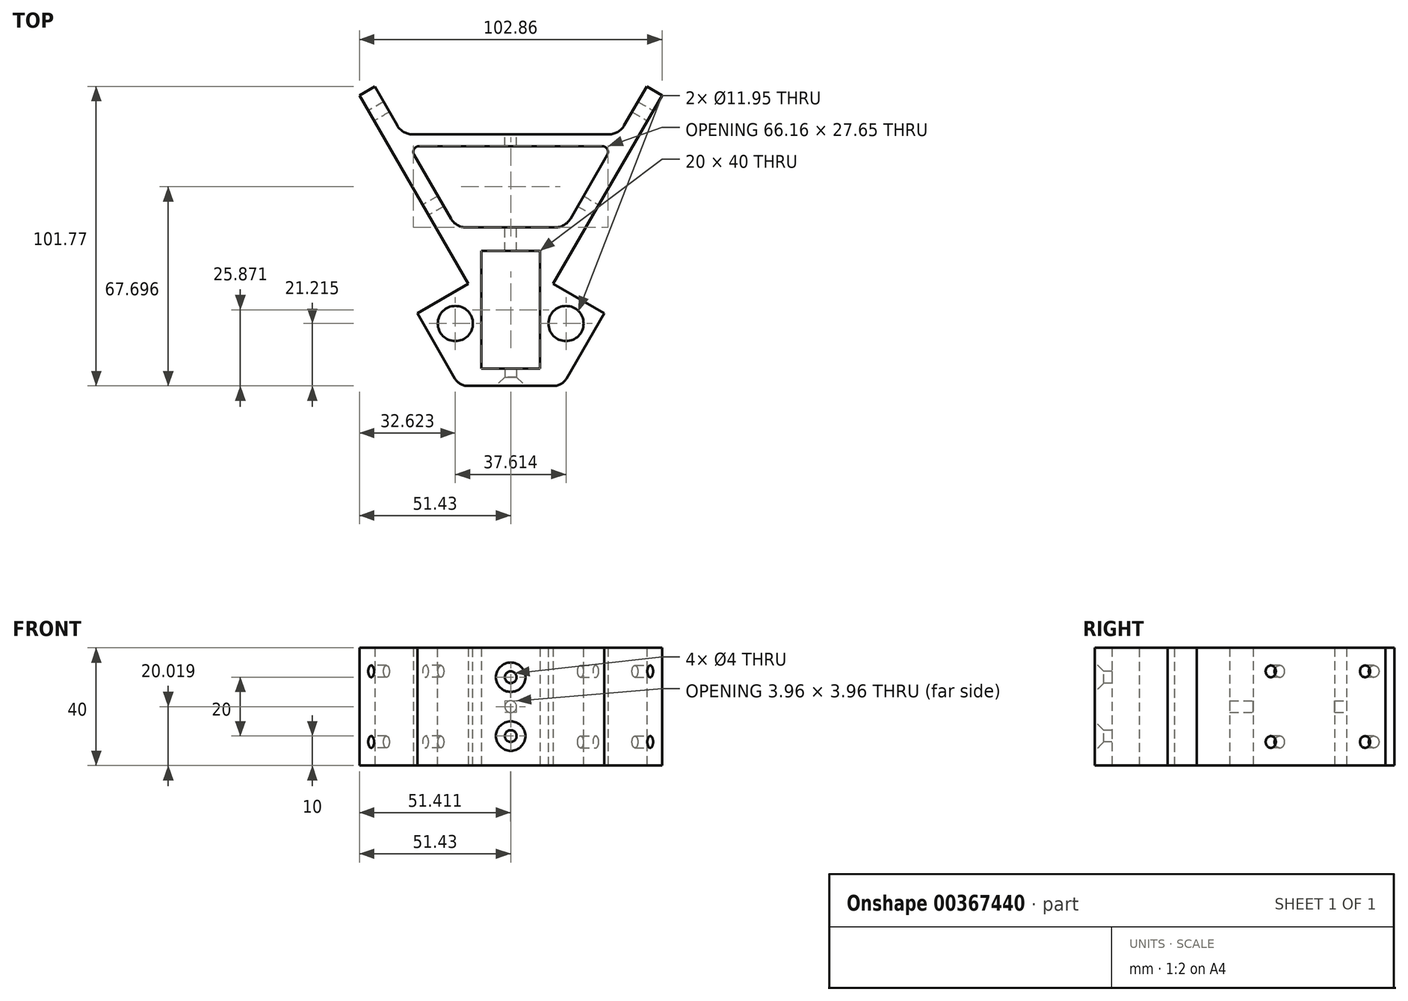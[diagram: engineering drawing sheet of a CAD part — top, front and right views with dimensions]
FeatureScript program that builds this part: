
annotation { "Feature Type Name" : "Feature", "Feature Type Description" : "" }
export const myFeature = defineFeature(function(context is Context, id is Id, definition is map)
    precondition{}
    {
        {
            var Q0;
            Q0=qCreatedBy(makeId("Top.planeOp"),FACE);
            var sketch = newSketch(context, id + "F0", { "sketchPlane" : qUnion([Q0])});
            skLineSegment(sketch, "E0", {"start": v(17.5, 30.31) * mm, "end": v(31.75, 55) * mm});
            skLineSegment(sketch, "E1", {"start": v(-17.5, 30.31) * mm, "end": v(-31.75, 55) * mm});
            skLineSegment(sketch, "E2", {"start": v(-17.5, 30.31) * mm, "end": v(17.5, 30.31) * mm});
            skLineSegment(sketch, "E3", {"start": v(-31.75, 55) * mm, "end": v(-14.43, 65) * mm});
            skLineSegment(sketch, "E4", {"start": v(-14.43, 65) * mm, "end": v(-51.43, 129.08) * mm});
            skLineSegment(sketch, "E5", {"start": v(-51.43, 129.08) * mm, "end": v(-46.23, 132.08) * mm});
            skLineSegment(sketch, "E6", {"start": v(31.75, 55) * mm, "end": v(14.43, 65) * mm});
            skLineSegment(sketch, "E7", {"start": v(14.43, 65) * mm, "end": v(51.43, 129.08) * mm});
            skLineSegment(sketch, "E8", {"start": v(51.43, 129.08) * mm, "end": v(46.23, 132.08) * mm});
            skLineSegment(sketch, "E9", {"start": v(-46.23, 132.08) * mm, "end": v(-36.85, 115.83) * mm});
            skLineSegment(sketch, "E10", {"start": v(18.58, 84.18) * mm, "end": v(34.54, 111.83) * mm});
            skLineSegment(sketch, "E11.bottom", {"start": v(-10, 36.18) * mm, "end": v(10, 36.18) * mm});
            skLineSegment(sketch, "E11.top", {"start": v(-10, 76.18) * mm, "end": v(10, 76.18) * mm});
            skLineSegment(sketch, "E11.left", {"start": v(-10, 36.18) * mm, "end": v(-10, 76.18) * mm});
            skLineSegment(sketch, "E11.right", {"start": v(10, 36.18) * mm, "end": v(10, 76.18) * mm});
            skLineSegment(sketch, "E12", {"start": v(36.85, 115.83) * mm, "end": v(-36.85, 115.83) * mm});
            skLineSegment(sketch, "E13.trimOffspring", {"start": v(36.85, 115.83) * mm, "end": v(46.23, 132.08) * mm});
            skLineSegment(sketch, "E14.trimOffspring", {"start": v(-34.54, 111.83) * mm, "end": v(-18.58, 84.18) * mm});
            skLineSegment(sketch, "E15", {"start": v(-34.54, 111.83) * mm, "end": v(34.54, 111.83) * mm});
            skLineSegment(sketch, "E16", {"start": v(18.58, 84.18) * mm, "end": v(-18.58, 84.18) * mm});
            skSolve(sketch);
        }
        {
            var Q0;
            Q0=qSketchRegion(id+"F0",true);
            extrude(context, id + "F1", {"entities" : qUnion([Q0]), "depth" : 40 * mm});
        }
        {
            var Q0;
            Q0=makeQuery(id+"F1.opExtrude","SWEPT_EDGE",EDGE,{"disambiguationData":[OSD([sQuery(id+"F0.wireOp",EDGE,"E1"),sQuery(id+"F0.wireOp",EDGE,"E2")])]});
            var Q1;
            Q1=makeQuery(id+"F1.opExtrude","SWEPT_EDGE",EDGE,{"disambiguationData":[OSD([sQuery(id+"F0.wireOp",EDGE,"E0"),sQuery(id+"F0.wireOp",EDGE,"E2")])]});
            fillet(context, id + "F2", {"entities" : qUnion([Q0, Q1]), "radius" : 5 * mm, "tangentPropagation" : true, "allowEdgeOverflow" : false});
        }
        {
            var Q0;
            Q0=makeQuery(id+"F1.opExtrude","SWEPT_EDGE",EDGE,{"disambiguationData":[OSD([sQuery(id+"F0.wireOp",EDGE,"E10"),sQuery(id+"F0.wireOp",EDGE,"E16")])]});
            var Q1;
            Q1=makeQuery(id+"F1.opExtrude","SWEPT_EDGE",EDGE,{"disambiguationData":[OSD([sQuery(id+"F0.wireOp",EDGE,"E14.trimOffspring"),sQuery(id+"F0.wireOp",EDGE,"E16")])]});
            var Q2;
            Q2=makeQuery(id+"F1.opExtrude","SWEPT_EDGE",EDGE,{"disambiguationData":[OSD([sQuery(id+"F0.wireOp",EDGE,"E9"),sQuery(id+"F0.wireOp",EDGE,"E12")])]});
            var Q3;
            Q3=makeQuery(id+"F1.opExtrude","SWEPT_EDGE",EDGE,{"disambiguationData":[OSD([sQuery(id+"F0.wireOp",EDGE,"E12"),sQuery(id+"F0.wireOp",EDGE,"E13.trimOffspring")])]});
            fillet(context, id + "F3", {"entities" : qUnion([Q0, Q1, Q2, Q3]), "radius" : 6 * mm, "tangentPropagation" : true, "allowEdgeOverflow" : false});
        }
        {
            var Q0;
            Q0=makeQuery(id+"F1.opExtrude","SWEPT_EDGE",EDGE,{"disambiguationData":[OSD([sQuery(id+"F0.wireOp",EDGE,"E10"),sQuery(id+"F0.wireOp",EDGE,"E15")])]});
            var Q1;
            Q1=makeQuery(id+"F1.opExtrude","SWEPT_EDGE",EDGE,{"disambiguationData":[OSD([sQuery(id+"F0.wireOp",EDGE,"E14.trimOffspring"),sQuery(id+"F0.wireOp",EDGE,"E15")])]});
            fillet(context, id + "F4", {"entities" : qUnion([Q0, Q1]), "radius" : 2 * mm, "tangentPropagation" : true, "allowEdgeOverflow" : false});
        }
        {
            var Q0;
            Q0=makeQuery(id+"F1.opExtrude","CAP_FACE",FACE,{"disambiguationData":[OSD([sQuery(id+"F0.wireOp",EDGE,"E0"),sQuery(id+"F0.wireOp",EDGE,"E1"),sQuery(id+"F0.wireOp",EDGE,"E2"),sQuery(id+"F0.wireOp",EDGE,"E3"),sQuery(id+"F0.wireOp",EDGE,"E4"),sQuery(id+"F0.wireOp",EDGE,"E5"),sQuery(id+"F0.wireOp",EDGE,"E6"),sQuery(id+"F0.wireOp",EDGE,"E7"),sQuery(id+"F0.wireOp",EDGE,"E8"),sQuery(id+"F0.wireOp",EDGE,"E9"),sQuery(id+"F0.wireOp",EDGE,"E10"),sQuery(id+"F0.wireOp",EDGE,"E11.bottom"),sQuery(id+"F0.wireOp",EDGE,"E11.top"),sQuery(id+"F0.wireOp",EDGE,"E11.left"),sQuery(id+"F0.wireOp",EDGE,"E11.right"),sQuery(id+"F0.wireOp",EDGE,"E12"),sQuery(id+"F0.wireOp",EDGE,"E13.trimOffspring"),sQuery(id+"F0.wireOp",EDGE,"E14.trimOffspring"),sQuery(id+"F0.wireOp",EDGE,"E15"),sQuery(id+"F0.wireOp",EDGE,"E16")])],"isStart":false});
            var sketch = newSketch(context, id + "F5", { "sketchPlane" : qUnion([Q0])});
            skCircle(sketch, "E17", {"center": v(-18.8, 51.52) * mm, "radius": 5.97 * mm});
            skCircle(sketch, "E18", {"center": v(18.8, 51.52) * mm, "radius": 5.97 * mm});
            skSolve(sketch);
        }
        {
            var Q0;
            Q0=qSketchRegion(id+"F5",true);
            extrude(context, id + "F6", {"entities" : qUnion([Q0]), "operationType" : NewBodyOperationType.REMOVE, "endBound" : BoundingType.THROUGH_ALL, "oppositeDirection" : true, "depth" : 25 * mm});
        }
        {
            var Q0;
            Q0=makeQuery(id+"F1.opExtrude","SWEPT_FACE",FACE,{"disambiguationData":[OSD([sQuery(id+"F0.wireOp",EDGE,"E12")])]});
            var sketch = newSketch(context, id + "F7", { "sketchPlane" : qUnion([Q0])});
            skPoint(sketch, "E19", {"position": v(0, 20) * mm});
            skPoint(sketch, "E19.positionSnap0", {"position": v(-33.39, 20) * mm});
            skSolve(sketch);
        }
        {
            var Q0;
            Q0=sQuery(id+"F7.wireOp",VERTEX,"E19");
            var Q1;
            Q1=makeQuery(id+"F1.opExtrude","SWEPT_BODY",BODY,{"disambiguationData":[OSD([sQuery(id+"F0.wireOp",EDGE,"E0"),sQuery(id+"F0.wireOp",EDGE,"E1"),sQuery(id+"F0.wireOp",EDGE,"E2"),sQuery(id+"F0.wireOp",EDGE,"E3"),sQuery(id+"F0.wireOp",EDGE,"E4"),sQuery(id+"F0.wireOp",EDGE,"E5"),sQuery(id+"F0.wireOp",EDGE,"E6"),sQuery(id+"F0.wireOp",EDGE,"E7"),sQuery(id+"F0.wireOp",EDGE,"E8"),sQuery(id+"F0.wireOp",EDGE,"E9"),sQuery(id+"F0.wireOp",EDGE,"E10"),sQuery(id+"F0.wireOp",EDGE,"E11.bottom"),sQuery(id+"F0.wireOp",EDGE,"E11.top"),sQuery(id+"F0.wireOp",EDGE,"E11.left"),sQuery(id+"F0.wireOp",EDGE,"E11.right"),sQuery(id+"F0.wireOp",EDGE,"E12"),sQuery(id+"F0.wireOp",EDGE,"E13.trimOffspring"),sQuery(id+"F0.wireOp",EDGE,"E14.trimOffspring"),sQuery(id+"F0.wireOp",EDGE,"E15"),sQuery(id+"F0.wireOp",EDGE,"E16")])]});
            hole(context, id + "F8", {"style" : HoleStyle.SIMPLE, "endStyle" : HoleEndStyle.BLIND, "holeDiameter" : 4 * mm, "holeDepth" : 40 * mm, "locations" : qUnion([Q0]), "scope" : qUnion([Q1])});
        }
        {
            var Q0;
            Q0=makeQuery(id+"F1.opExtrude","SWEPT_FACE",FACE,{"disambiguationData":[OSD([sQuery(id+"F0.wireOp",EDGE,"E7")])]});
            var sketch = newSketch(context, id + "F9", { "sketchPlane" : qUnion([Q0])});
            skPoint(sketch, "E20", {"position": v(129.5, 32) * mm});
            skPoint(sketch, "E21", {"position": v(129.5, 8) * mm});
            skPoint(sketch, "E22", {"position": v(92.5, 8) * mm});
            skPoint(sketch, "E23", {"position": v(92.5, 32) * mm});
            skSolve(sketch);
        }
        {
            var Q0;
            Q0=sQuery(id+"F9.wireOp",VERTEX,"E20");
            var Q1;
            Q1=sQuery(id+"F9.wireOp",VERTEX,"E23");
            var Q2;
            Q2=sQuery(id+"F9.wireOp",VERTEX,"E22");
            var Q3;
            Q3=sQuery(id+"F9.wireOp",VERTEX,"E21");
            var Q4;
            Q4=makeQuery(id+"F1.opExtrude","SWEPT_BODY",BODY,{"disambiguationData":[OSD([sQuery(id+"F0.wireOp",EDGE,"E0"),sQuery(id+"F0.wireOp",EDGE,"E1"),sQuery(id+"F0.wireOp",EDGE,"E2"),sQuery(id+"F0.wireOp",EDGE,"E3"),sQuery(id+"F0.wireOp",EDGE,"E4"),sQuery(id+"F0.wireOp",EDGE,"E5"),sQuery(id+"F0.wireOp",EDGE,"E6"),sQuery(id+"F0.wireOp",EDGE,"E7"),sQuery(id+"F0.wireOp",EDGE,"E8"),sQuery(id+"F0.wireOp",EDGE,"E9"),sQuery(id+"F0.wireOp",EDGE,"E10"),sQuery(id+"F0.wireOp",EDGE,"E11.bottom"),sQuery(id+"F0.wireOp",EDGE,"E11.top"),sQuery(id+"F0.wireOp",EDGE,"E11.left"),sQuery(id+"F0.wireOp",EDGE,"E11.right"),sQuery(id+"F0.wireOp",EDGE,"E12"),sQuery(id+"F0.wireOp",EDGE,"E13.trimOffspring"),sQuery(id+"F0.wireOp",EDGE,"E14.trimOffspring"),sQuery(id+"F0.wireOp",EDGE,"E15"),sQuery(id+"F0.wireOp",EDGE,"E16")])]});
            hole(context, id + "F10", {"style" : HoleStyle.SIMPLE, "endStyle" : HoleEndStyle.BLIND, "holeDiameter" : 4 * mm, "holeDepth" : 12 * mm, "locations" : qUnion([Q0, Q1, Q2, Q3]), "scope" : qUnion([Q4])});
        }
        {
            var Q0;
            Q0=makeQuery(id+"F1.opExtrude","SWEPT_FACE",FACE,{"disambiguationData":[OSD([sQuery(id+"F0.wireOp",EDGE,"E4")])]});
            var sketch = newSketch(context, id + "F11", { "sketchPlane" : qUnion([Q0])});
            skPoint(sketch, "E24", {"position": v(-129.5, 32) * mm});
            skPoint(sketch, "E25", {"position": v(-129.5, 8) * mm});
            skPoint(sketch, "E26", {"position": v(-92.5, 8) * mm});
            skPoint(sketch, "E27", {"position": v(-92.5, 32) * mm});
            skSolve(sketch);
        }
        {
            var Q0;
            Q0=sQuery(id+"F11.wireOp",VERTEX,"E24");
            var Q1;
            Q1=sQuery(id+"F11.wireOp",VERTEX,"E25");
            var Q2;
            Q2=sQuery(id+"F11.wireOp",VERTEX,"E26");
            var Q3;
            Q3=sQuery(id+"F11.wireOp",VERTEX,"E27");
            var Q4;
            Q4=makeQuery(id+"F1.opExtrude","SWEPT_BODY",BODY,{"disambiguationData":[OSD([sQuery(id+"F0.wireOp",EDGE,"E0"),sQuery(id+"F0.wireOp",EDGE,"E1"),sQuery(id+"F0.wireOp",EDGE,"E2"),sQuery(id+"F0.wireOp",EDGE,"E3"),sQuery(id+"F0.wireOp",EDGE,"E4"),sQuery(id+"F0.wireOp",EDGE,"E5"),sQuery(id+"F0.wireOp",EDGE,"E6"),sQuery(id+"F0.wireOp",EDGE,"E7"),sQuery(id+"F0.wireOp",EDGE,"E8"),sQuery(id+"F0.wireOp",EDGE,"E9"),sQuery(id+"F0.wireOp",EDGE,"E10"),sQuery(id+"F0.wireOp",EDGE,"E11.bottom"),sQuery(id+"F0.wireOp",EDGE,"E11.top"),sQuery(id+"F0.wireOp",EDGE,"E11.left"),sQuery(id+"F0.wireOp",EDGE,"E11.right"),sQuery(id+"F0.wireOp",EDGE,"E12"),sQuery(id+"F0.wireOp",EDGE,"E13.trimOffspring"),sQuery(id+"F0.wireOp",EDGE,"E14.trimOffspring"),sQuery(id+"F0.wireOp",EDGE,"E15"),sQuery(id+"F0.wireOp",EDGE,"E16")])]});
            hole(context, id + "F12", {"style" : HoleStyle.SIMPLE, "endStyle" : HoleEndStyle.BLIND, "holeDiameter" : 4 * mm, "holeDepth" : 12 * mm, "locations" : qUnion([Q0, Q1, Q2, Q3]), "scope" : qUnion([Q4])});
        }
        {
            var Q0;
            Q0=makeQuery(id+"F1.opExtrude","SWEPT_FACE",FACE,{"disambiguationData":[OSD([sQuery(id+"F0.wireOp",EDGE,"E2")])]});
            var sketch = newSketch(context, id + "F13", { "sketchPlane" : qUnion([Q0])});
            skPoint(sketch, "E28", {"position": v(0, 30) * mm});
            skPoint(sketch, "E28.positionSnap0", {"position": v(0, 40) * mm});
            skPoint(sketch, "E29", {"position": v(0, 10) * mm});
            skPoint(sketch, "E29.positionSnap0", {"position": v(0, 0) * mm});
            skSolve(sketch);
        }
        {
            var Q0;
            Q0=sQuery(id+"F13.wireOp",VERTEX,"E28");
            var Q1;
            Q1=sQuery(id+"F13.wireOp",VERTEX,"E29");
            var Q2;
            Q2=makeQuery(id+"F1.opExtrude","SWEPT_BODY",BODY,{"disambiguationData":[OSD([sQuery(id+"F0.wireOp",EDGE,"E0"),sQuery(id+"F0.wireOp",EDGE,"E1"),sQuery(id+"F0.wireOp",EDGE,"E2"),sQuery(id+"F0.wireOp",EDGE,"E3"),sQuery(id+"F0.wireOp",EDGE,"E4"),sQuery(id+"F0.wireOp",EDGE,"E5"),sQuery(id+"F0.wireOp",EDGE,"E6"),sQuery(id+"F0.wireOp",EDGE,"E7"),sQuery(id+"F0.wireOp",EDGE,"E8"),sQuery(id+"F0.wireOp",EDGE,"E9"),sQuery(id+"F0.wireOp",EDGE,"E10"),sQuery(id+"F0.wireOp",EDGE,"E11.bottom"),sQuery(id+"F0.wireOp",EDGE,"E11.top"),sQuery(id+"F0.wireOp",EDGE,"E11.left"),sQuery(id+"F0.wireOp",EDGE,"E11.right"),sQuery(id+"F0.wireOp",EDGE,"E12"),sQuery(id+"F0.wireOp",EDGE,"E13.trimOffspring"),sQuery(id+"F0.wireOp",EDGE,"E14.trimOffspring"),sQuery(id+"F0.wireOp",EDGE,"E15"),sQuery(id+"F0.wireOp",EDGE,"E16")])]});
            hole(context, id + "F14", {"style" : HoleStyle.C_SINK, "endStyle" : HoleEndStyle.BLIND, "holeDiameter" : 4 * mm, "cSinkDiameter" : 10 * mm, "cSinkAngle" : 90 * degree, "holeDepth" : 12 * mm, "locations" : qUnion([Q0, Q1]), "scope" : qUnion([Q2])});
        }
    });
